# Revit family: 63_UN_LED Panel_Backlit Panel 60x60_Natec
name_source: partatom
category: Lighting Fixtures
units: mm (PartAtom-declared; Revit-internal decimal feet)

## family parameters
Always vertical = Yes
Cut with Voids When Loaded = No
Light Source = Yes
OmniClass Number = 23.80.70.11.14.11
OmniClass Title = Downlights
Part Type = Normal
Room Calculation Point = Yes
Round Connector Dimension = Use Diameter
Shared = No
Work Plane-Based = No

## types (1)
- 8068-0099 60x 60 3000K UGR19
    Apparent Load = 29 VA
    Assembly Code = 63.0
    Calc_L1_Symbol = 6 mm  [stored 0.019685 ft]
    Calc_L2_Symbol = 6 mm  [stored 0.019685 ft]
    Color Filter = 16777215
    Dimming Lamp Color Temperature Shift = <None>
    H1 = 33 mm  [stored 0.108268 ft]
    Housing_Material = Laminate, White
    IfcExportAs = IfcLightFixtureType
    IfcExportType = USERDEFINED
    L1 = 595 mm
    L2 = 595 mm
    L3 = 20 mm  [stored 0.0656168 ft]
    LED Panel = Yes
    Lamp = LED
    Luminous Flux (lm) = 3749 lm
    Manufacturer = Natec Lighting
    Model = Backlit Panel
    Photometric Web File = 8068-0099 60x 60 3000K UGR19.IES
    Tilt Angle = 90.00°
    Type Comments = 60x60
    URL = https://nateclighting.nl
    Voltage = 230 V
    Wattage Comments = 28.8W

note: [stored X ft] marks values corroborated as IEEE doubles in the binary element streams (Revit-internal decimal feet)

## geometry (parser evidence)
native form markers: Sweep x4
no freeform markers — native parametric forms only
